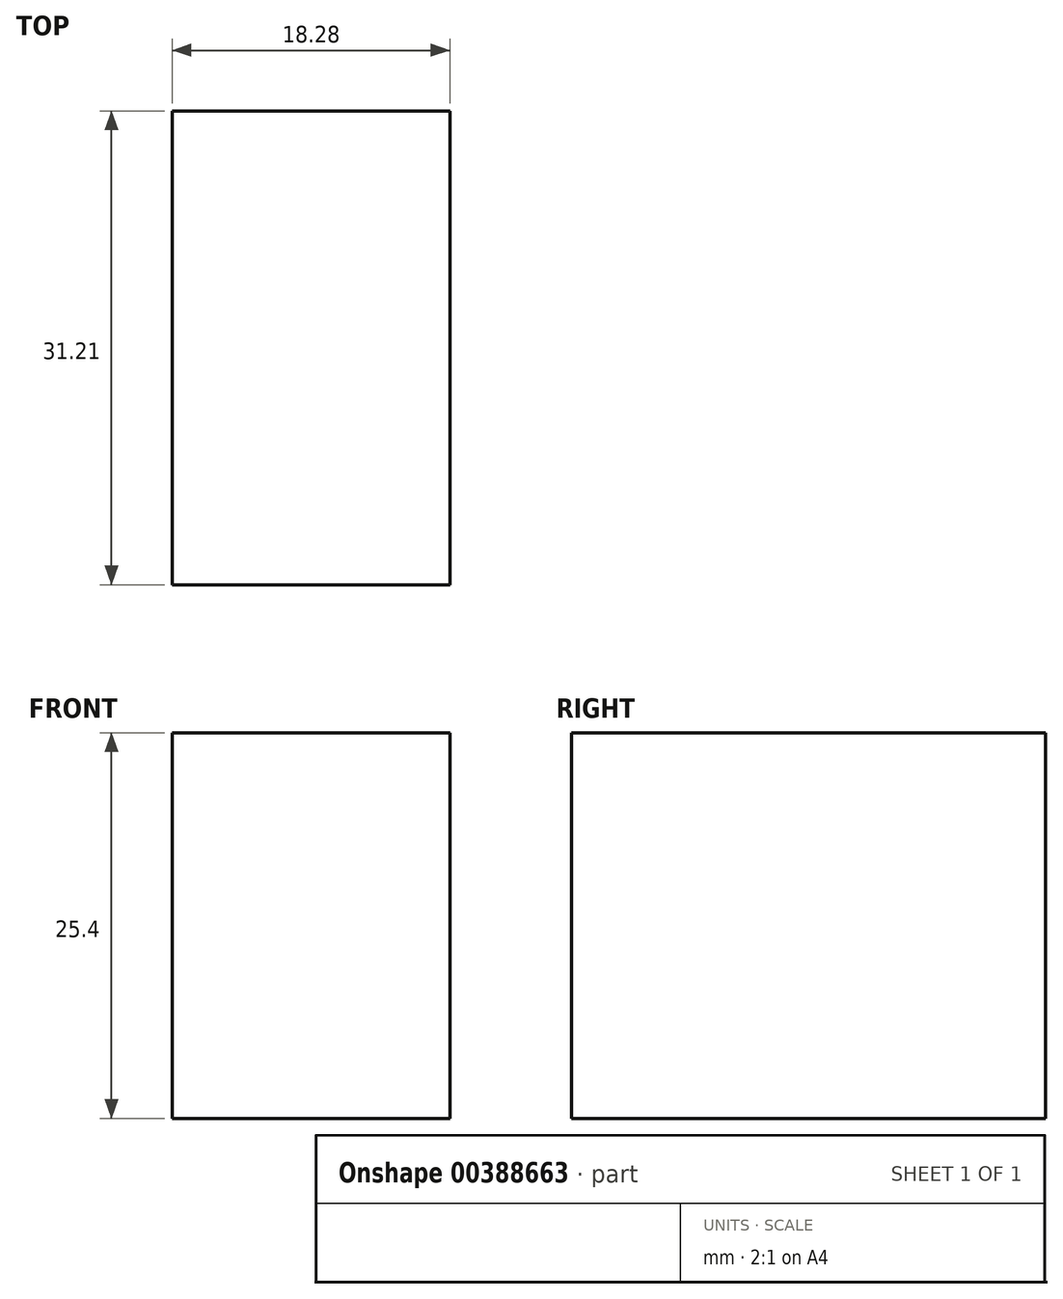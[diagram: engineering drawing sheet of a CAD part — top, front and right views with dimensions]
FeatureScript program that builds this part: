
annotation { "Feature Type Name" : "Feature", "Feature Type Description" : "" }
export const myFeature = defineFeature(function(context is Context, id is Id, definition is map)
    precondition{}
    {
        {
            var Q0;
            Q0=qCreatedBy(makeId("Top.planeOp"),FACE);
            var sketch = newSketch(context, id + "F0", { "sketchPlane" : qUnion([Q0])});
            skLineSegment(sketch, "E0", {"start": v(0, 0) * mm, "end": v(0, 31.2) * mm});
            skLineSegment(sketch, "E1", {"start": v(0, 31.2) * mm, "end": v(18.28, 31.2) * mm});
            skLineSegment(sketch, "E2", {"start": v(18.28, 31.2) * mm, "end": v(18.28, 0) * mm});
            skLineSegment(sketch, "E3", {"start": v(18.28, 0) * mm, "end": v(0, 0) * mm});
            skSolve(sketch);
        }
        {
            var Q0;
            Q0 = qSketchRegion(id + "F0", true);
            extrude(context, id + "F1", {"entities" : qUnion([Q0]), "depth" : 25.4 * mm});
        }
    });
